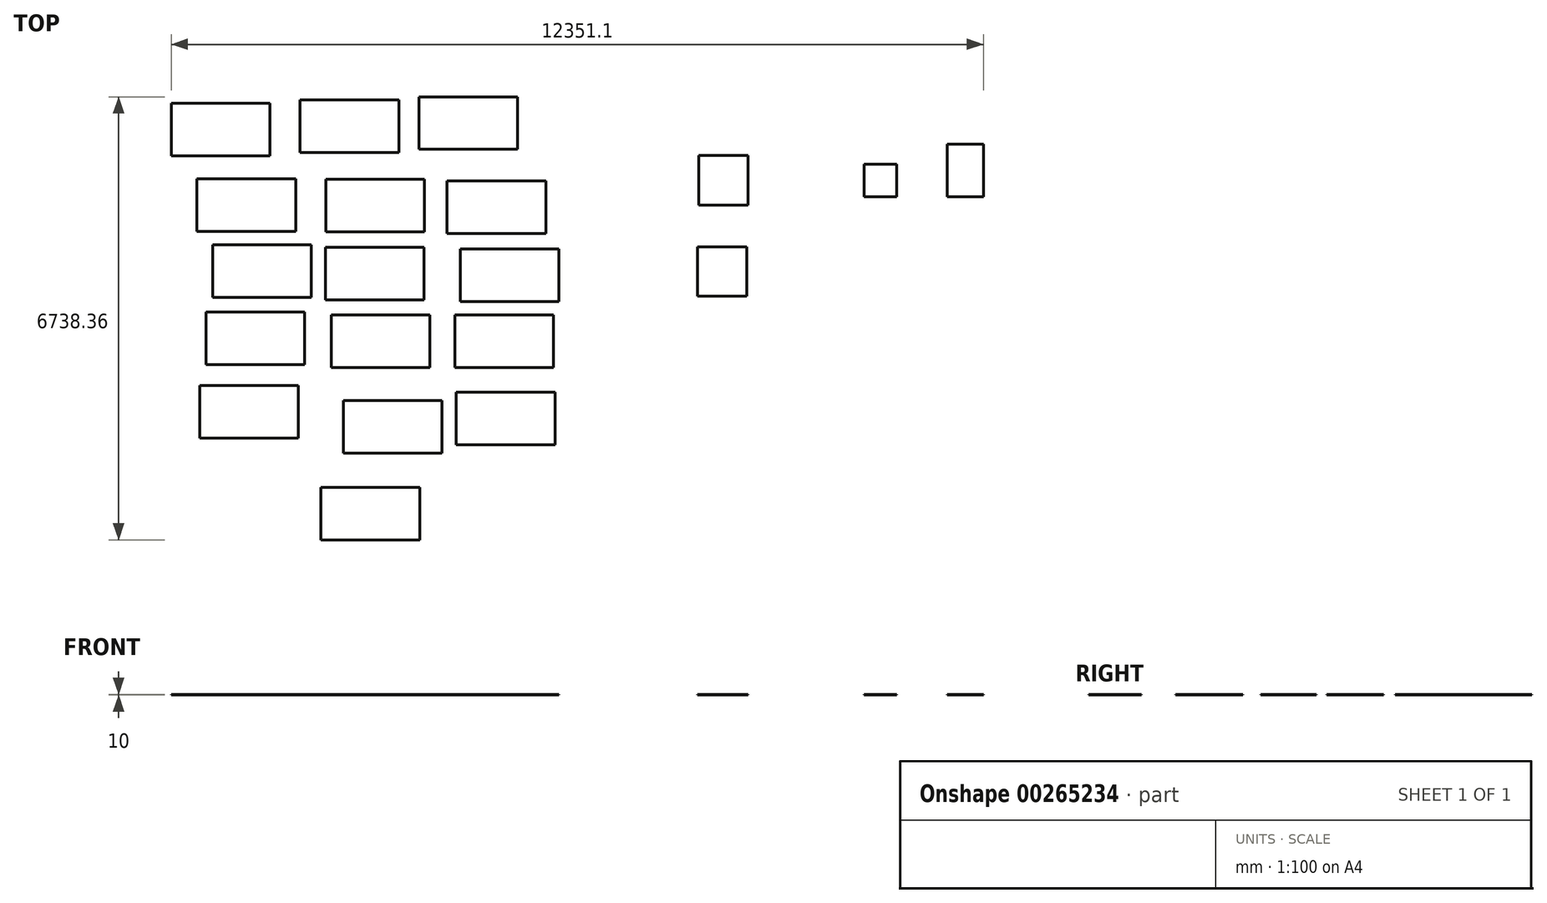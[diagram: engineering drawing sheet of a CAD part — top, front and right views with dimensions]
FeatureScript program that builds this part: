
annotation { "Feature Type Name" : "Feature", "Feature Type Description" : "" }
export const myFeature = defineFeature(function(context is Context, id is Id, definition is map)
    precondition{}
    {
        {
            var Q0;
            Q0=qCreatedBy(makeId("Top.planeOp"),FACE);
            var sketch = newSketch(context, id + "F0", { "sketchPlane" : qUnion([Q0])});
            skLineSegment(sketch, "E0.bottom", {"start": v(1119.7, 118.02) * mm, "end": v(-380.3, 118.02) * mm});
            skLineSegment(sketch, "E0.top", {"start": v(1119.7, 918.02) * mm, "end": v(-380.3, 918.02) * mm});
            skLineSegment(sketch, "E0.left", {"start": v(1119.7, 118.02) * mm, "end": v(1119.7, 918.02) * mm});
            skLineSegment(sketch, "E0.right", {"start": v(-380.3, 118.02) * mm, "end": v(-380.3, 918.02) * mm});
            skPoint(sketch, "E0.middle", {"position": v(369.7, 518.02) * mm});
            skLineSegment(sketch, "E1.bottom", {"start": v(727.1, 1326.5) * mm, "end": v(-772.9, 1326.5) * mm});
            skLineSegment(sketch, "E1.top", {"start": v(727.1, 2126.5) * mm, "end": v(-772.9, 2126.5) * mm});
            skLineSegment(sketch, "E1.left", {"start": v(727.1, 1326.5) * mm, "end": v(727.1, 2126.5) * mm});
            skLineSegment(sketch, "E1.right", {"start": v(-772.9, 1326.5) * mm, "end": v(-772.9, 2126.5) * mm});
            skPoint(sketch, "E1.middle", {"position": v(-22.9, 1726.5) * mm});
            skLineSegment(sketch, "E2.bottom", {"start": v(2532.9, 1372.1) * mm, "end": v(1032.9, 1372.1) * mm});
            skLineSegment(sketch, "E2.top", {"start": v(2532.9, 2172.1) * mm, "end": v(1032.9, 2172.1) * mm});
            skLineSegment(sketch, "E2.left", {"start": v(2532.9, 1372.1) * mm, "end": v(2532.9, 2172.1) * mm});
            skLineSegment(sketch, "E2.right", {"start": v(1032.9, 1372.1) * mm, "end": v(1032.9, 2172.1) * mm});
            skPoint(sketch, "E2.middle", {"position": v(1782.9, 1772.1) * mm});
            skLineSegment(sketch, "E3.bottom", {"start": v(2961.54, 95.27) * mm, "end": v(1461.54, 95.27) * mm});
            skLineSegment(sketch, "E3.top", {"start": v(2961.54, 895.27) * mm, "end": v(1461.54, 895.27) * mm});
            skLineSegment(sketch, "E3.left", {"start": v(2961.54, 95.27) * mm, "end": v(2961.54, 895.27) * mm});
            skLineSegment(sketch, "E3.right", {"start": v(1461.54, 95.27) * mm, "end": v(1461.54, 895.27) * mm});
            skPoint(sketch, "E3.middle", {"position": v(2211.54, 495.27) * mm});
            skLineSegment(sketch, "E4.bottom", {"start": v(-841.56, 122.63) * mm, "end": v(-2341.56, 122.63) * mm});
            skLineSegment(sketch, "E4.top", {"start": v(-841.56, 922.63) * mm, "end": v(-2341.56, 922.63) * mm});
            skLineSegment(sketch, "E4.left", {"start": v(-841.56, 122.63) * mm, "end": v(-841.56, 922.63) * mm});
            skLineSegment(sketch, "E4.right", {"start": v(-2341.56, 122.63) * mm, "end": v(-2341.56, 922.63) * mm});
            skPoint(sketch, "E4.middle", {"position": v(-1591.56, 522.63) * mm});
            skLineSegment(sketch, "E5.bottom", {"start": v(-1233.72, 1271.77) * mm, "end": v(-2733.72, 1271.77) * mm});
            skLineSegment(sketch, "E5.top", {"start": v(-1233.72, 2071.77) * mm, "end": v(-2733.72, 2071.77) * mm});
            skLineSegment(sketch, "E5.left", {"start": v(-1233.72, 1271.77) * mm, "end": v(-1233.72, 2071.77) * mm});
            skLineSegment(sketch, "E5.right", {"start": v(-2733.72, 1271.77) * mm, "end": v(-2733.72, 2071.77) * mm});
            skPoint(sketch, "E5.middle", {"position": v(-1983.72, 1671.77) * mm});
            skLineSegment(sketch, "E6.bottom", {"start": v(-604.8, -877.98) * mm, "end": v(-2104.8, -877.98) * mm});
            skLineSegment(sketch, "E6.top", {"start": v(-604.8, -77.98) * mm, "end": v(-2104.8, -77.98) * mm});
            skLineSegment(sketch, "E6.left", {"start": v(-604.8, -877.98) * mm, "end": v(-604.8, -77.98) * mm});
            skLineSegment(sketch, "E6.right", {"start": v(-2104.8, -877.98) * mm, "end": v(-2104.8, -77.98) * mm});
            skPoint(sketch, "E6.middle", {"position": v(-1354.8, -477.98) * mm});
            skLineSegment(sketch, "E7.bottom", {"start": v(1109.78, -914.46) * mm, "end": v(-390.22, -914.46) * mm});
            skLineSegment(sketch, "E7.top", {"start": v(1109.78, -114.46) * mm, "end": v(-390.22, -114.46) * mm});
            skLineSegment(sketch, "E7.left", {"start": v(1109.78, -914.46) * mm, "end": v(1109.78, -114.46) * mm});
            skLineSegment(sketch, "E7.right", {"start": v(-390.22, -914.46) * mm, "end": v(-390.22, -114.46) * mm});
            skPoint(sketch, "E7.middle", {"position": v(359.78, -514.46) * mm});
            skLineSegment(sketch, "E8.bottom", {"start": v(3161.81, -941.82) * mm, "end": v(1661.81, -941.82) * mm});
            skLineSegment(sketch, "E8.top", {"start": v(3161.81, -141.82) * mm, "end": v(1661.81, -141.82) * mm});
            skLineSegment(sketch, "E8.left", {"start": v(3161.81, -941.82) * mm, "end": v(3161.81, -141.82) * mm});
            skLineSegment(sketch, "E8.right", {"start": v(1661.81, -941.82) * mm, "end": v(1661.81, -141.82) * mm});
            skPoint(sketch, "E8.middle", {"position": v(2411.81, -541.82) * mm});
            skLineSegment(sketch, "E9.bottom", {"start": v(3080.1, -1947.64) * mm, "end": v(1580.1, -1947.64) * mm});
            skLineSegment(sketch, "E9.top", {"start": v(3080.1, -1147.64) * mm, "end": v(1580.1, -1147.64) * mm});
            skLineSegment(sketch, "E9.left", {"start": v(3080.1, -1947.64) * mm, "end": v(3080.1, -1147.64) * mm});
            skLineSegment(sketch, "E9.right", {"start": v(1580.1, -1947.64) * mm, "end": v(1580.1, -1147.64) * mm});
            skPoint(sketch, "E9.middle", {"position": v(2330.1, -1547.64) * mm});
            skLineSegment(sketch, "E10.bottom", {"start": v(1201.35, -1947.64) * mm, "end": v(-298.65, -1947.64) * mm});
            skLineSegment(sketch, "E10.top", {"start": v(1201.35, -1147.64) * mm, "end": v(-298.65, -1147.64) * mm});
            skLineSegment(sketch, "E10.left", {"start": v(1201.35, -1947.64) * mm, "end": v(1201.35, -1147.64) * mm});
            skLineSegment(sketch, "E10.right", {"start": v(-298.65, -1947.64) * mm, "end": v(-298.65, -1147.64) * mm});
            skPoint(sketch, "E10.middle", {"position": v(451.35, -1547.64) * mm});
            skLineSegment(sketch, "E11.bottom", {"start": v(-704.75, -1902.03) * mm, "end": v(-2204.75, -1902.03) * mm});
            skLineSegment(sketch, "E11.top", {"start": v(-704.75, -1102.03) * mm, "end": v(-2204.75, -1102.03) * mm});
            skLineSegment(sketch, "E11.left", {"start": v(-704.75, -1902.03) * mm, "end": v(-704.75, -1102.03) * mm});
            skLineSegment(sketch, "E11.right", {"start": v(-2204.75, -1902.03) * mm, "end": v(-2204.75, -1102.03) * mm});
            skPoint(sketch, "E11.middle", {"position": v(-1454.75, -1502.03) * mm});
            skLineSegment(sketch, "E12.bottom", {"start": v(-797.82, -3020.48) * mm, "end": v(-2297.82, -3020.48) * mm});
            skLineSegment(sketch, "E12.top", {"start": v(-797.82, -2220.48) * mm, "end": v(-2297.82, -2220.48) * mm});
            skLineSegment(sketch, "E12.left", {"start": v(-797.82, -3020.48) * mm, "end": v(-797.82, -2220.48) * mm});
            skLineSegment(sketch, "E12.right", {"start": v(-2297.82, -3020.48) * mm, "end": v(-2297.82, -2220.48) * mm});
            skPoint(sketch, "E12.middle", {"position": v(-1547.82, -2620.48) * mm});
            skLineSegment(sketch, "E13.bottom", {"start": v(1382.66, -3245.7) * mm, "end": v(-117.34, -3245.7) * mm});
            skLineSegment(sketch, "E13.top", {"start": v(1382.66, -2445.7) * mm, "end": v(-117.34, -2445.7) * mm});
            skLineSegment(sketch, "E13.left", {"start": v(1382.66, -3245.7) * mm, "end": v(1382.66, -2445.7) * mm});
            skLineSegment(sketch, "E13.right", {"start": v(-117.34, -3245.7) * mm, "end": v(-117.34, -2445.7) * mm});
            skPoint(sketch, "E13.middle", {"position": v(632.66, -2845.7) * mm});
            skLineSegment(sketch, "E14.bottom", {"start": v(3102.48, -3122.85) * mm, "end": v(1602.48, -3122.85) * mm});
            skLineSegment(sketch, "E14.top", {"start": v(3102.48, -2322.85) * mm, "end": v(1602.48, -2322.85) * mm});
            skLineSegment(sketch, "E14.left", {"start": v(3102.48, -3122.85) * mm, "end": v(3102.48, -2322.85) * mm});
            skLineSegment(sketch, "E14.right", {"start": v(1602.48, -3122.85) * mm, "end": v(1602.48, -2322.85) * mm});
            skPoint(sketch, "E14.middle", {"position": v(2352.48, -2722.85) * mm});
            skLineSegment(sketch, "E15.bottom", {"start": v(1044.84, -4566.27) * mm, "end": v(-455.16, -4566.27) * mm});
            skLineSegment(sketch, "E15.top", {"start": v(1044.84, -3766.27) * mm, "end": v(-455.16, -3766.27) * mm});
            skLineSegment(sketch, "E15.left", {"start": v(1044.84, -4566.27) * mm, "end": v(1044.84, -3766.27) * mm});
            skLineSegment(sketch, "E15.right", {"start": v(-455.16, -4566.27) * mm, "end": v(-455.16, -3766.27) * mm});
            skPoint(sketch, "E15.middle", {"position": v(294.84, -4166.27) * mm});
            skLineSegment(sketch, "E16.bottom", {"start": v(5290.37, 1277.13) * mm, "end": v(6040.37, 1277.13) * mm});
            skLineSegment(sketch, "E16.top", {"start": v(5290.37, 527.13) * mm, "end": v(6040.37, 527.13) * mm});
            skLineSegment(sketch, "E16.left", {"start": v(5290.37, 1277.13) * mm, "end": v(5290.37, 527.13) * mm});
            skLineSegment(sketch, "E16.right", {"start": v(6040.37, 1277.13) * mm, "end": v(6040.37, 527.13) * mm});
            skLineSegment(sketch, "E17.bottom", {"start": v(8301.27, 648.87) * mm, "end": v(7801.27, 648.87) * mm});
            skLineSegment(sketch, "E17.top", {"start": v(8301.27, 1148.87) * mm, "end": v(7801.27, 1148.87) * mm});
            skLineSegment(sketch, "E17.left", {"start": v(8301.27, 648.87) * mm, "end": v(8301.27, 1148.87) * mm});
            skLineSegment(sketch, "E17.right", {"start": v(7801.27, 648.87) * mm, "end": v(7801.27, 1148.87) * mm});
            skPoint(sketch, "E17.middle", {"position": v(8051.27, 898.87) * mm});
            skLineSegment(sketch, "E18.bottom", {"start": v(9617.35, 648.87) * mm, "end": v(9067.35, 648.87) * mm});
            skLineSegment(sketch, "E18.top", {"start": v(9617.35, 1448.87) * mm, "end": v(9067.35, 1448.87) * mm});
            skLineSegment(sketch, "E18.left", {"start": v(9617.35, 648.87) * mm, "end": v(9617.35, 1448.87) * mm});
            skLineSegment(sketch, "E18.right", {"start": v(9067.35, 648.87) * mm, "end": v(9067.35, 1448.87) * mm});
            skPoint(sketch, "E18.middle", {"position": v(9342.35, 1048.87) * mm});
            skLineSegment(sketch, "E19.bottom", {"start": v(6019.1, -860.7) * mm, "end": v(5269.1, -860.7) * mm});
            skLineSegment(sketch, "E19.top", {"start": v(6019.1, -110.7) * mm, "end": v(5269.1, -110.7) * mm});
            skLineSegment(sketch, "E19.left", {"start": v(6019.1, -860.7) * mm, "end": v(6019.1, -110.7) * mm});
            skLineSegment(sketch, "E19.right", {"start": v(5269.1, -860.7) * mm, "end": v(5269.1, -110.7) * mm});
            skPoint(sketch, "E19.middle", {"position": v(5644.1, -485.7) * mm});
            skSolve(sketch);
        }
        {
            var Q0;
            Q0=makeQuery(id+"F0.imprint","IMPRINT",FACE,{"disambiguationData":[TD([[makeQuery(id+"F0.imprint","IMPRINT",EDGE,{"derivedFrom":sQuery(id+"F0.wireOp",EDGE,"E4.bottom")}),-1.0]])]});
            var Q1;
            Q1=makeQuery(id+"F0.imprint","IMPRINT",FACE,{"disambiguationData":[TD([[makeQuery(id+"F0.imprint","IMPRINT",EDGE,{"derivedFrom":sQuery(id+"F0.wireOp",EDGE,"E13.bottom")}),-1.0]])]});
            var Q2;
            Q2=makeQuery(id+"F0.imprint","IMPRINT",FACE,{"disambiguationData":[TD([[makeQuery(id+"F0.imprint","IMPRINT",EDGE,{"derivedFrom":sQuery(id+"F0.wireOp",EDGE,"E9.bottom")}),-1.0]])]});
            var Q3;
            Q3=makeQuery(id+"F0.imprint","IMPRINT",FACE,{"disambiguationData":[TD([[makeQuery(id+"F0.imprint","IMPRINT",EDGE,{"derivedFrom":sQuery(id+"F0.wireOp",EDGE,"E11.bottom")}),-1.0]])]});
            var Q4;
            Q4=makeQuery(id+"F0.imprint","IMPRINT",FACE,{"disambiguationData":[TD([[makeQuery(id+"F0.imprint","IMPRINT",EDGE,{"derivedFrom":sQuery(id+"F0.wireOp",EDGE,"E1.bottom")}),-1.0]])]});
            var Q5;
            Q5=makeQuery(id+"F0.imprint","IMPRINT",FACE,{"disambiguationData":[TD([[makeQuery(id+"F0.imprint","IMPRINT",EDGE,{"derivedFrom":sQuery(id+"F0.wireOp",EDGE,"E14.bottom")}),-1.0]])]});
            var Q6;
            Q6=makeQuery(id+"F0.imprint","IMPRINT",FACE,{"disambiguationData":[TD([[makeQuery(id+"F0.imprint","IMPRINT",EDGE,{"derivedFrom":sQuery(id+"F0.wireOp",EDGE,"E10.bottom")}),-1.0]])]});
            var Q7;
            Q7=makeQuery(id+"F0.imprint","IMPRINT",FACE,{"disambiguationData":[TD([[makeQuery(id+"F0.imprint","IMPRINT",EDGE,{"derivedFrom":sQuery(id+"F0.wireOp",EDGE,"E15.bottom")}),-1.0]])]});
            var Q8;
            Q8=makeQuery(id+"F0.imprint","IMPRINT",FACE,{"disambiguationData":[TD([[makeQuery(id+"F0.imprint","IMPRINT",EDGE,{"derivedFrom":sQuery(id+"F0.wireOp",EDGE,"E8.bottom")}),-1.0]])]});
            var Q9;
            Q9=makeQuery(id+"F0.imprint","IMPRINT",FACE,{"disambiguationData":[TD([[makeQuery(id+"F0.imprint","IMPRINT",EDGE,{"derivedFrom":sQuery(id+"F0.wireOp",EDGE,"E7.bottom")}),-1.0]])]});
            var Q10;
            Q10=makeQuery(id+"F0.imprint","IMPRINT",FACE,{"disambiguationData":[TD([[makeQuery(id+"F0.imprint","IMPRINT",EDGE,{"derivedFrom":sQuery(id+"F0.wireOp",EDGE,"E2.bottom")}),-1.0]])]});
            var Q11;
            Q11=makeQuery(id+"F0.imprint","IMPRINT",FACE,{"disambiguationData":[TD([[makeQuery(id+"F0.imprint","IMPRINT",EDGE,{"derivedFrom":sQuery(id+"F0.wireOp",EDGE,"E0.bottom")}),-1.0]])]});
            var Q12;
            Q12=makeQuery(id+"F0.imprint","IMPRINT",FACE,{"disambiguationData":[TD([[makeQuery(id+"F0.imprint","IMPRINT",EDGE,{"derivedFrom":sQuery(id+"F0.wireOp",EDGE,"E3.bottom")}),-1.0]])]});
            var Q13;
            Q13=makeQuery(id+"F0.imprint","IMPRINT",FACE,{"disambiguationData":[TD([[makeQuery(id+"F0.imprint","IMPRINT",EDGE,{"derivedFrom":sQuery(id+"F0.wireOp",EDGE,"E6.bottom")}),-1.0]])]});
            var Q14;
            Q14=makeQuery(id+"F0.imprint","IMPRINT",FACE,{"disambiguationData":[TD([[makeQuery(id+"F0.imprint","IMPRINT",EDGE,{"derivedFrom":sQuery(id+"F0.wireOp",EDGE,"E12.bottom")}),-1.0]])]});
            var Q15;
            Q15=makeQuery(id+"F0.imprint","IMPRINT",FACE,{"disambiguationData":[TD([[makeQuery(id+"F0.imprint","IMPRINT",EDGE,{"derivedFrom":sQuery(id+"F0.wireOp",EDGE,"E5.bottom")}),-1.0]])]});
            var Q16;
            Q16=makeQuery(id+"F0.imprint","IMPRINT",FACE,{"disambiguationData":[TD([[makeQuery(id+"F0.imprint","IMPRINT",EDGE,{"derivedFrom":sQuery(id+"F0.wireOp",EDGE,"E16.bottom")}),-1.0]])]});
            var Q17;
            Q17=makeQuery(id+"F0.imprint","IMPRINT",FACE,{"disambiguationData":[TD([[makeQuery(id+"F0.imprint","IMPRINT",EDGE,{"derivedFrom":sQuery(id+"F0.wireOp",EDGE,"E19.bottom")}),-1.0]])]});
            var Q18;
            Q18=makeQuery(id+"F0.imprint","IMPRINT",FACE,{"disambiguationData":[TD([[makeQuery(id+"F0.imprint","IMPRINT",EDGE,{"derivedFrom":sQuery(id+"F0.wireOp",EDGE,"E18.bottom")}),-1.0]])]});
            var Q19;
            Q19=makeQuery(id+"F0.imprint","IMPRINT",FACE,{"disambiguationData":[TD([[makeQuery(id+"F0.imprint","IMPRINT",EDGE,{"derivedFrom":sQuery(id+"F0.wireOp",EDGE,"E17.bottom")}),-1.0]])]});
            extrude(context, id + "F1", {"entities" : qUnion([Q0, Q1, Q2, Q3, Q4, Q5, Q6, Q7, Q8, Q9, Q10, Q11, Q12, Q13, Q14, Q15, Q16, Q17, Q18, Q19]), "depth" : 10 * mm});
        }
    });
